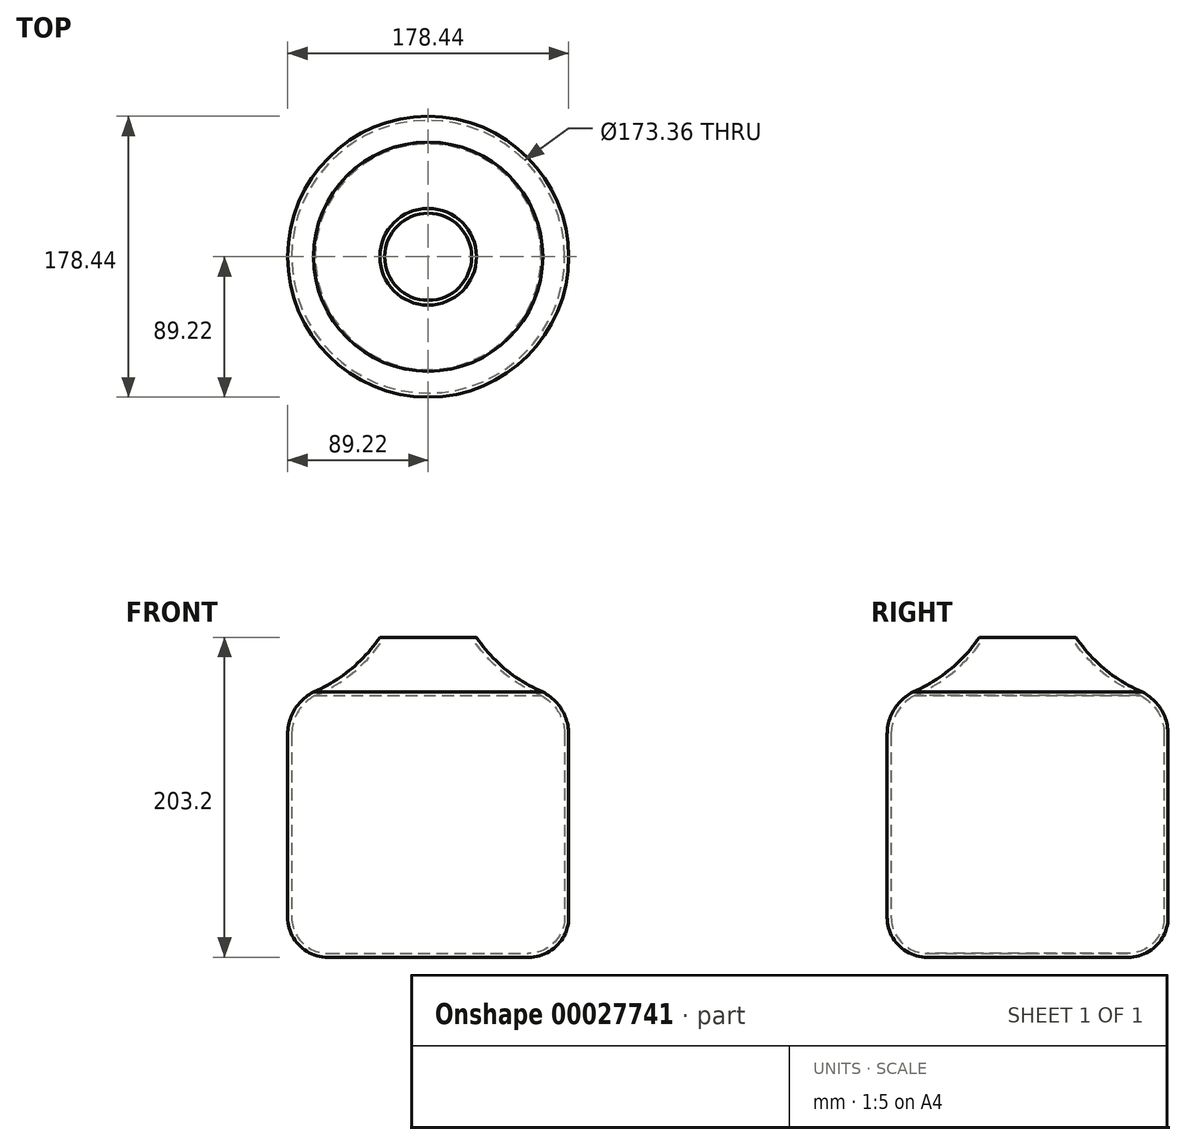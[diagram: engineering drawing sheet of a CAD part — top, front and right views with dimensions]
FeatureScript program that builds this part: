
annotation { "Feature Type Name" : "Feature", "Feature Type Description" : "" }
export const myFeature = defineFeature(function(context is Context, id is Id, definition is map)
    precondition{}
    {
        {
            var Q0;
            Q0=qCreatedBy(makeId("Front.planeOp"),FACE);
            var sketch = newSketch(context, id + "F0", { "sketchPlane" : qUnion([Q0])});
            skLineSegment(sketch, "E0", {"start": v(0, 0) * mm, "end": v(63.82, 0) * mm});
            skLineSegment(sketch, "E1", {"start": v(89.22, 25.4) * mm, "end": v(89.22, 141.61) * mm});
            skArc(sketch, "E2", {"start": v(89.22, 141.61) * mm, "mid": v(84.78, 157.36) * mm, "end": v(72.79, 168.5) * mm});
            skArc(sketch, "E3", {"start": v(30.7, 203.2) * mm, "mid": v(49.22, 182.8) * mm, "end": v(72.79, 168.5) * mm});
            skLineSegment(sketch, "E4", {"start": v(30.7, 203.2) * mm, "end": v(0, 203.2) * mm});
            skLineSegment(sketch, "E5", {"start": v(0, 203.2) * mm, "end": v(0, 0) * mm});
            skLineSegment(sketch, "E6", {"start": v(0, -48.16) * mm, "end": v(0, 208.66) * mm, "construction": true});
            skPoint(sketch, "E7.visualSharp", {"position": v(89.22, 0) * mm});
            skArc(sketch, "E7.filletArc", {"start": v(63.82, 0) * mm, "mid": v(81.78, 7.44) * mm, "end": v(89.22, 25.4) * mm});
            skSolve(sketch);
        }
        {
            var Q0;
            Q0 = qSketchRegion(id + "F0", true);
            var Q1;
            Q1=sQuery(id+"F0.wireOp",EDGE,"E6");
            revolve(context, id + "F1", {"entities" : qUnion([Q0]), "axis" : qUnion([Q1]), "revolveType" : RevolveType.FULL});
        }
        {
            var Q0;
            Q0=makeQuery(id+"F1.opRevolve","SWEPT_FACE",FACE,{"disambiguationData":[OSD([sQuery(id+"F0.wireOp",EDGE,"E4")])]});
            shell(context, id + "F2", {"entities" : qUnion([Q0]), "thickness" : 2.54 * mm});
        }
    });
